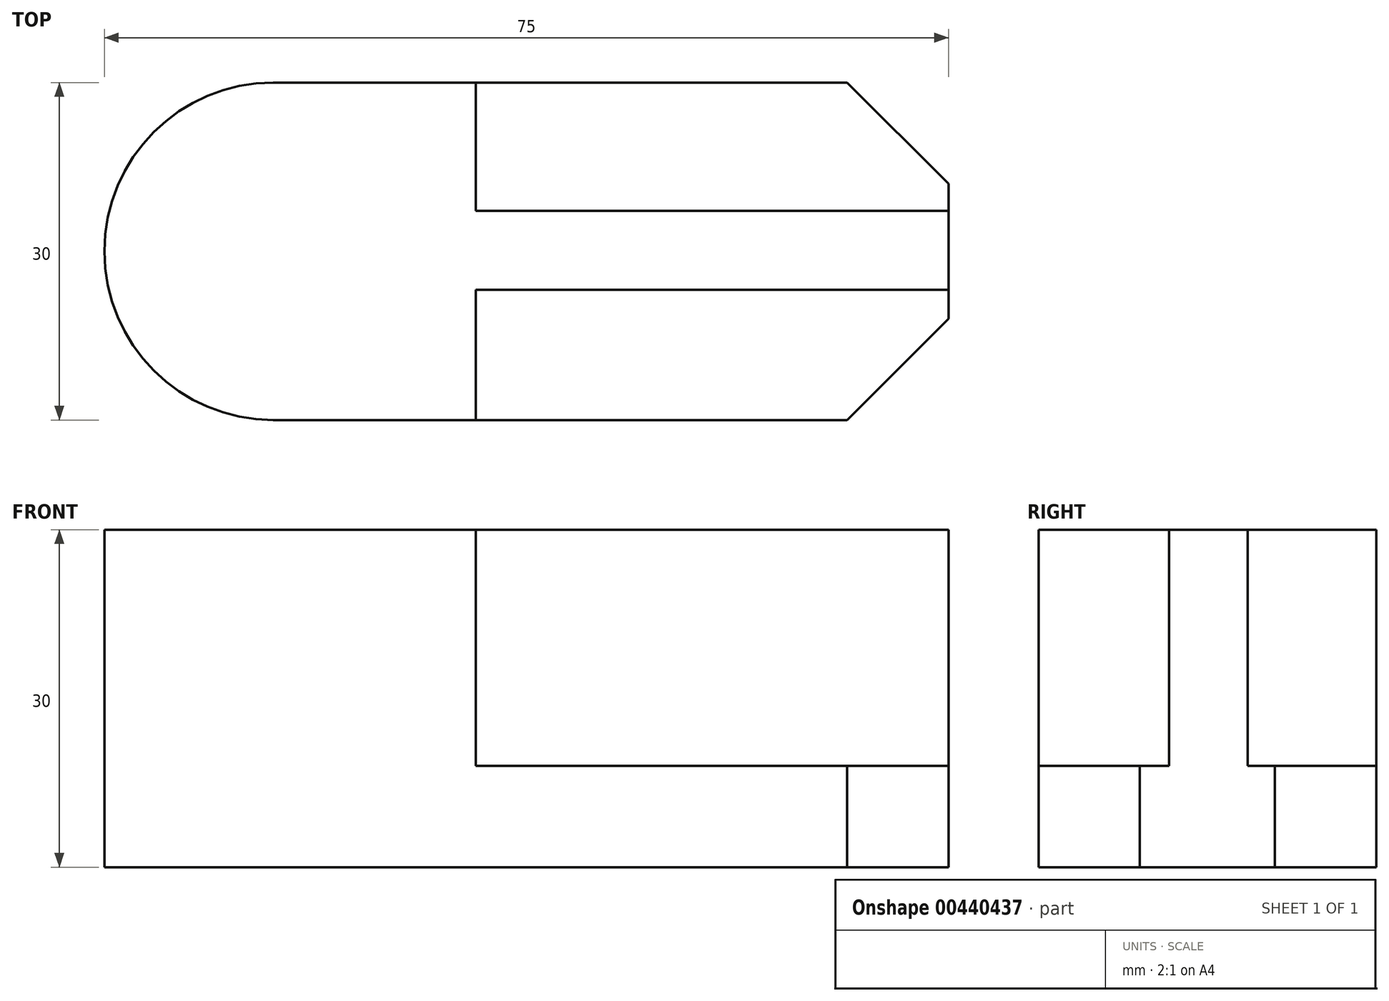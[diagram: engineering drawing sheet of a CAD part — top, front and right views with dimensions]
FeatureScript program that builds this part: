
annotation { "Feature Type Name" : "Feature", "Feature Type Description" : "" }
export const myFeature = defineFeature(function(context is Context, id is Id, definition is map)
    precondition{}
    {
        {
            var Q0;
            Q0=qCreatedBy(makeId("Top.planeOp"),FACE);
            var sketch = newSketch(context, id + "F0", { "sketchPlane" : qUnion([Q0])});
            skLineSegment(sketch, "E0.bottom", {"start": v(0, 0) * mm, "end": v(-51, 0) * mm});
            skLineSegment(sketch, "E0.top", {"start": v(0, 30) * mm, "end": v(-51, 30) * mm});
            skLineSegment(sketch, "E1", {"start": v(0, 30) * mm, "end": v(9, 21) * mm});
            skLineSegment(sketch, "E2", {"start": v(9, 21) * mm, "end": v(9, 9) * mm});
            skLineSegment(sketch, "E3", {"start": v(9, 9) * mm, "end": v(0, 0) * mm});
            skArc(sketch, "E4", {"start": v(-51, 30) * mm, "mid": v(-66, 15) * mm, "end": v(-51, 0) * mm});
            skSolve(sketch);
        }
        {
            var Q0;
            Q0=makeQuery(id+"F0.imprint","IMPRINT",FACE,{"disambiguationData":[TD([[makeQuery(id+"F0.imprint","IMPRINT",EDGE,{"derivedFrom":sQuery(id+"F0.wireOp",EDGE,"E0.bottom")}),-1.0]])]});
            extrude(context, id + "F1", {"entities" : qUnion([Q0]), "depth" : 9 * mm});
        }
        {
            var Q0;
            Q0=makeQuery(id+"F1.opExtrude","CAP_FACE",FACE,{"disambiguationData":[OSD([sQuery(id+"F0.wireOp",EDGE,"E0.bottom"),sQuery(id+"F0.wireOp",EDGE,"E0.top"),sQuery(id+"F0.wireOp",EDGE,"E1"),sQuery(id+"F0.wireOp",EDGE,"E2"),sQuery(id+"F0.wireOp",EDGE,"E3"),sQuery(id+"F0.wireOp",EDGE,"E4")])],"isStart":false});
            var sketch = newSketch(context, id + "F2", { "sketchPlane" : qUnion([Q0])});
            skLineSegment(sketch, "E5", {"start": v(-33, 30) * mm, "end": v(-33, 18.58) * mm});
            skLineSegment(sketch, "E6", {"start": v(9, 18.58) * mm, "end": v(-33, 18.58) * mm});
            skLineSegment(sketch, "E7", {"start": v(-33, 11.58) * mm, "end": v(9, 11.58) * mm});
            skPoint(sketch, "E8.start.orphan", {"position": v(-51, 30) * mm});
            skLineSegment(sketch, "E9.trimOffspring", {"start": v(-33, 11.58) * mm, "end": v(-33, 0) * mm});
            skSolve(sketch);
        }
        {
            var Q0;
            {var subQ4=sQuery(id+"F2.wireOp",EDGE,"E5");Q0=makeQuery(id+"F2.imprint","IMPRINT",FACE,{"disambiguationData":[TD([[makeQuery(id+"F2.imprint","IMPRINT",EDGE,{"derivedFrom":subQ4}),-1.0]])]});}
            extrude(context, id + "F3", {"entities" : qUnion([Q0]), "operationType" : NewBodyOperationType.ADD, "depth" : 21 * mm});
        }
    });
